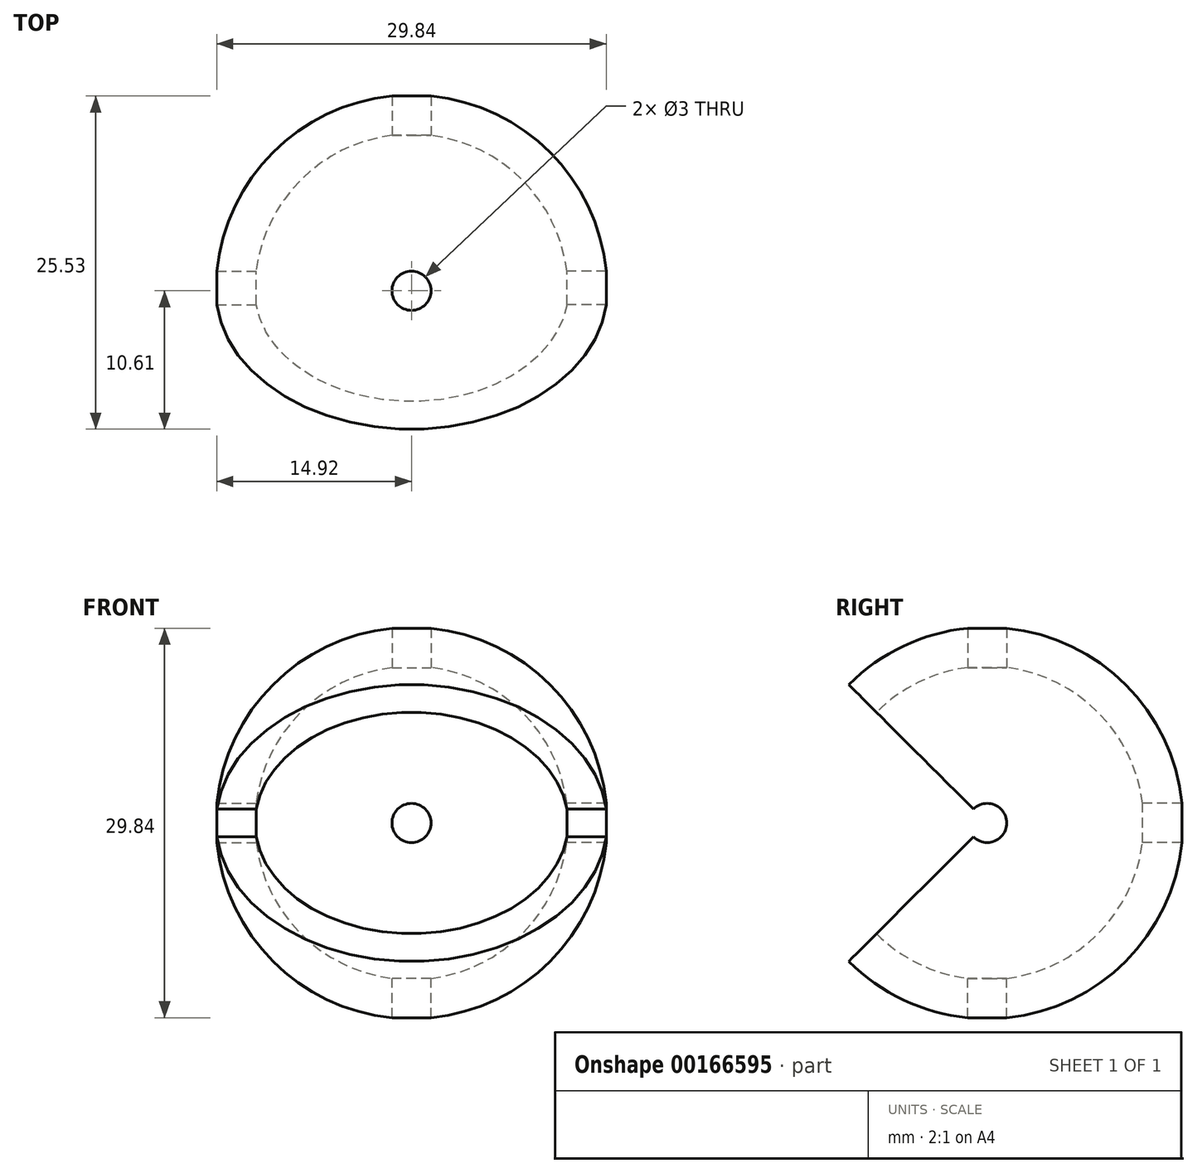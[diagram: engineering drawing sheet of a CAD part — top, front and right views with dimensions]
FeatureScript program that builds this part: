
annotation { "Feature Type Name" : "Feature", "Feature Type Description" : "" }
export const myFeature = defineFeature(function(context is Context, id is Id, definition is map)
    precondition{}
    {
        {
            var Q0;
            Q0=qCreatedBy(makeId("Top.planeOp"),FACE);
            var sketch = newSketch(context, id + "F0", { "sketchPlane" : qUnion([Q0])});
            skLineSegment(sketch, "E0", {"start": v(-17.64, 0) * mm, "end": v(18.78, 0) * mm});
            skArc(sketch, "E1", {"start": v(15, 0) * mm, "mid": v(0, 15) * mm, "end": v(-15, 0) * mm});
            skSolve(sketch);
        }
        {
            var Q0;
            {var subQ0=sQuery(id+"F0.wireOp",EDGE,"E1");Q0=makeQuery(id+"F0.imprint","IMPRINT",FACE,{"disambiguationData":[TD([[makeQuery(id+"F0.imprint","IMPRINT",EDGE,{"derivedFrom":subQ0}),1.0]])]});}
            var Q1;
            Q1=sQuery(id+"F0.wireOp",EDGE,"E0");
            revolve(context, id + "F1", {"entities" : qUnion([Q0]), "axis" : qUnion([Q1]), "revolveType" : RevolveType.ONE_DIRECTION, "angle" : 270 * degree});
        }
        {
            var Q0;
            Q0=makeQuery(id+"F1.opRevolve","CAP_FACE",FACE,{"disambiguationData":[OSD([sQuery(id+"F0.wireOp",EDGE,"E0"),sQuery(id+"F0.wireOp",EDGE,"E1")])],"isStart":true});
            var Q1;
            Q1=makeQuery(id+"F1.opRevolve","CAP_FACE",FACE,{"disambiguationData":[OSD([sQuery(id+"F0.wireOp",EDGE,"E0"),sQuery(id+"F0.wireOp",EDGE,"E1")])],"isStart":false});
            var Q2;
            Q2=makeQuery(id+"F1.opRevolve","SWEPT_BODY",BODY,{"disambiguationData":[OSD([sQuery(id+"F0.wireOp",EDGE,"E0"),sQuery(id+"F0.wireOp",EDGE,"E1")])]});
            shell(context, id + "F14", {"entities" : qUnion([Q0, Q1]), "parts" : qUnion([Q2]), "thickness" : 3 * mm});
        }
        {
            var Q0;
            Q0=qCreatedBy(makeId("Right.planeOp"),FACE);
            var sketch = newSketch(context, id + "F2", { "sketchPlane" : qUnion([Q0])});
            skPoint(sketch, "E2", {"position": v(0, 0) * mm});
            skSolve(sketch);
        }
        {
            var Q0;
            Q0=sQuery(id+"F2.wireOp",VERTEX,"E2");
            var Q1;
            Q1=makeQuery(id+"F1.opRevolve","SWEPT_BODY",BODY,{"disambiguationData":[OSD([sQuery(id+"F0.wireOp",EDGE,"E0"),sQuery(id+"F0.wireOp",EDGE,"E1")])]});
            hole(context, id + "F3", {"style" : HoleStyle.SIMPLE, "endStyle" : HoleEndStyle.THROUGH, "holeDiameter" : 3 * mm, "locations" : qUnion([Q0]), "scope" : qUnion([Q1]), "isTappedThrough" : true});
        }
        {
            var Q0;
            Q0=qCreatedBy(makeId("Right.planeOp"),FACE);
            var sketch = newSketch(context, id + "F4", { "sketchPlane" : qUnion([Q0])});
            skPoint(sketch, "E3", {"position": v(0, 0) * mm});
            skSolve(sketch);
        }
        {
            var Q0;
            Q0=sQuery(id+"F4.wireOp",VERTEX,"E3");
            var Q1;
            Q1=makeQuery(id+"F1.opRevolve","SWEPT_BODY",BODY,{"disambiguationData":[OSD([sQuery(id+"F0.wireOp",EDGE,"E0"),sQuery(id+"F0.wireOp",EDGE,"E1")])]});
            hole(context, id + "F5", {"style" : HoleStyle.SIMPLE, "endStyle" : HoleEndStyle.THROUGH, "oppositeDirection" : true, "holeDiameter" : 3 * mm, "locations" : qUnion([Q0]), "scope" : qUnion([Q1]), "isTappedThrough" : true});
        }
        {
            var Q0;
            Q0=qCreatedBy(makeId("Top.planeOp"),FACE);
            var sketch = newSketch(context, id + "F6", { "sketchPlane" : qUnion([Q0])});
            skLineSegment(sketch, "E4", {"start": v(20, 0) * mm, "end": v(-20, 0) * mm});
            skPoint(sketch, "E5", {"position": v(13.42, 1.5) * mm});
            skPoint(sketch, "E6", {"position": v(-13.42, 1.5) * mm});
            skPoint(sketch, "E7", {"position": v(0, 0) * mm});
            skSolve(sketch);
        }
        {
            var Q0;
            Q0=makeQuery(id+"F1.opRevolve","SWEPT_BODY",BODY,{"disambiguationData":[OSD([sQuery(id+"F0.wireOp",EDGE,"E0"),sQuery(id+"F0.wireOp",EDGE,"E1")])]});
            var Q1;
            Q1=sQuery(id+"F6.wireOp",EDGE,"E4");
            var Q2;
            Q2=sQuery(id+"F6.wireOp",EDGE,"E4");
            transform(context, id + "F7", {"entities" : qUnion([Q0]), "transformType" : TransformType.ROTATION, "transformAxis" : qUnion([Q2]), "angle" : 135 * degree, "makeCopy" : false});
        }
        {
            var Q0;
            Q0=qCreatedBy(makeId("Front.planeOp"),FACE);
            var sketch = newSketch(context, id + "F8", { "sketchPlane" : qUnion([Q0])});
            skPoint(sketch, "E8", {"position": v(0, 0) * mm});
            skSolve(sketch);
        }
        {
            var Q0;
            Q0=sQuery(id+"F8.wireOp",VERTEX,"E8");
            var Q1;
            Q1=makeQuery(id+"F1.opRevolve","SWEPT_BODY",BODY,{"disambiguationData":[OSD([sQuery(id+"F0.wireOp",EDGE,"E0"),sQuery(id+"F0.wireOp",EDGE,"E1")])]});
            hole(context, id + "F9", {"style" : HoleStyle.SIMPLE, "endStyle" : HoleEndStyle.THROUGH, "holeDiameter" : 3 * mm, "locations" : qUnion([Q0]), "scope" : qUnion([Q1]), "isTappedThrough" : true});
        }
        {
            var Q0;
            Q0=qCreatedBy(makeId("Top.planeOp"),FACE);
            var sketch = newSketch(context, id + "F10", { "sketchPlane" : qUnion([Q0])});
            skPoint(sketch, "E9", {"position": v(0, 0) * mm});
            skSolve(sketch);
        }
        {
            var Q0;
            Q0=sQuery(id+"F10.wireOp",VERTEX,"E9");
            var Q1;
            Q1=makeQuery(id+"F1.opRevolve","SWEPT_BODY",BODY,{"disambiguationData":[OSD([sQuery(id+"F0.wireOp",EDGE,"E0"),sQuery(id+"F0.wireOp",EDGE,"E1")])]});
            hole(context, id + "F11", {"style" : HoleStyle.SIMPLE, "endStyle" : HoleEndStyle.THROUGH, "holeDiameter" : 3 * mm, "locations" : qUnion([Q0]), "scope" : qUnion([Q1]), "isTappedThrough" : true});
        }
        {
            var Q0;
            Q0=qCreatedBy(makeId("Top.planeOp"),FACE);
            var sketch = newSketch(context, id + "F12", { "sketchPlane" : qUnion([Q0])});
            skPoint(sketch, "E10", {"position": v(0, 0) * mm});
            skSolve(sketch);
        }
        {
            var Q0;
            Q0=sQuery(id+"F12.wireOp",VERTEX,"E10");
            var Q1;
            Q1=makeQuery(id+"F1.opRevolve","SWEPT_BODY",BODY,{"disambiguationData":[OSD([sQuery(id+"F0.wireOp",EDGE,"E0"),sQuery(id+"F0.wireOp",EDGE,"E1")])]});
            hole(context, id + "F13", {"style" : HoleStyle.SIMPLE, "endStyle" : HoleEndStyle.THROUGH, "oppositeDirection" : true, "holeDiameter" : 3 * mm, "locations" : qUnion([Q0]), "scope" : qUnion([Q1]), "isTappedThrough" : true});
        }
    });
